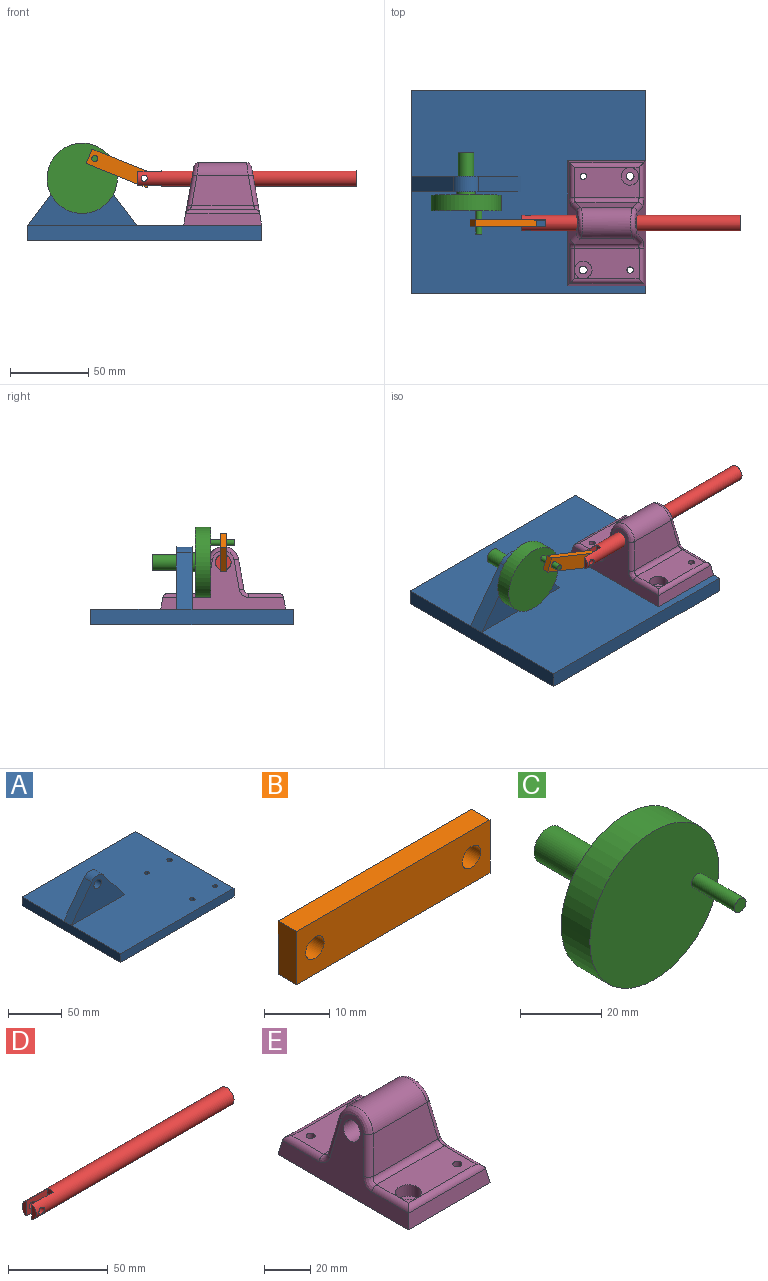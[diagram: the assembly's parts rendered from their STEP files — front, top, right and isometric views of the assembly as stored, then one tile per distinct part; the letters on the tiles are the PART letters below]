
ASSEMBLY  parts=5 mates=5
PART A: 16 faces, bbox 150x130x50 mm
  f0: plane 150x130mm, normal (0,0,1), area 18735.6mm2, adj f1,f3,f4,f5,f6,f10,f11,f12
  f1: plane 130x10mm, normal (-1,0,0), area 1300mm2, adj f0,f2,f4,f5,f8
  f2: plane 150x130mm, normal (0,0,-1), area 19435.6mm2, adj f1,f3,f4,f5,f12,f13,f14,f15
  f3: plane 130x10mm, normal (1,0,0), area 1300mm2, adj f0,f2,f4,f5
  f4: plane 150x10mm, normal (0,-1,0), area 1500mm2, adj f0,f1,f2,f3
  f5: plane 150x10mm, normal (0,1,0), area 1500mm2, adj f0,f1,f2,f3
  f6: plane 36x27mm, normal (0.8,0,0.6), area 450mm2, adj f0,f7,f10,f11
  f7: cylinder r=10mm len=16mm, axis (0,-1,0), area 185.5mm2, adj f6,f8,f10,f11
  f8: plane 36x27mm, normal (-0.8,0,0.6), area 450mm2, adj f1,f7,f10,f11
  f9: cylinder r=5mm len=10mm, axis (0,-1,0), area 314.2mm2, adj f10,f11
  f10: plane 70x40mm, normal (0,1,0), area 1514.2mm2, adj f0,f6,f7,f8,f9
  f11: plane 70x40mm, normal (0,-1,0), area 1514.2mm2, adj f0,f6,f7,f8,f9
  f12: cylinder r=2.5mm len=10mm, axis (0,0,1), area 157.1mm2, adj f0,f2
  f13: cylinder r=2.5mm len=10mm, axis (0,0,1), area 157.1mm2, adj f0,f2
  f14: cylinder r=2mm len=10mm, axis (0,0,1), area 125.7mm2, adj f0,f2
  f15: cylinder r=2mm len=10mm, axis (0,0,1), area 125.7mm2, adj f0,f2
PART B: 8 faces, bbox 42x4x10 mm
  f0: plane 42x10mm, normal (0,-1,0), area 394.9mm2, adj f1,f3,f4,f5,f6,f7
  f1: plane 42x4mm, normal (0,0,1), area 168mm2, adj f0,f2,f4,f5
  f2: plane 42x10mm, normal (0,1,0), area 394.9mm2, adj f1,f3,f4,f5,f6,f7
  f3: cylinder r=2mm len=4mm, axis (0,1,0), area 50.3mm2, adj f0,f2
  f4: plane 10x4mm, normal (-1,0,0), area 40mm2, adj f0,f1,f2,f6
  f5: plane 10x4mm, normal (1,0,0), area 40mm2, adj f0,f1,f2,f6
  f6: plane 42x4mm, normal (0,0,-1), area 168mm2, adj f0,f2,f4,f5
  f7: cylinder r=2mm len=4mm, axis (0,1,0), area 50.3mm2, adj f0,f2
PART C: 9 faces, bbox 45x52x45 mm
  f0: cylinder r=5mm len=25mm, axis (0,-1,0), area 785.4mm2, adj f1,f3
  f1: plane 10x10mm, normal (0,1,0), area 78.5mm2, adj f0
  f2: cylinder r=6mm len=12mm, axis (0,1,0), area 75.4mm2, adj f3,f6
  f3: plane 12x12mm, normal (0,1,0), area 34.6mm2, adj f0,f2
  f4: cylinder r=22.5mm len=45mm, axis (0,1,0), area 1413.7mm2, adj f5,f6
  f5: plane 45x45mm, normal (0,-1,0), area 1577.9mm2, adj f4,f7
  f6: plane 45x45mm, normal (0,1,0), area 1477.3mm2, adj f2,f4
  f7: cylinder r=2mm len=15mm, axis (0,1,0), area 188.5mm2, adj f5,f8
  f8: plane 4x4mm, normal (0,-1,0), area 12.6mm2, adj f7
PART D: 9 faces, bbox 140x10x10 mm
  f0: plane 9.17x3mm, normal (-1,0,0), area 19.8mm2, adj f1,f4
  f1: cylinder r=5mm len=140mm, axis (1,0,0), area 4249.1mm2, adj f0,f2,f3,f4,f5,f6,f7,f8
  f2: plane 9.17x3mm, normal (-1,0,0), area 19.8mm2, adj f1,f5
  f3: plane 10x10mm, normal (1,0,0), area 78.5mm2, adj f1
  f4: plane 15x9.17mm, normal (0,1,0), area 124.9mm2, adj f0,f1,f6,f8
  f5: plane 15x9.17mm, normal (0,-1,0), area 124.9mm2, adj f1,f2,f6,f7
  f6: plane 10x4mm, normal (-1,0,0), area 38.9mm2, adj f1,f4,f5
  f7: cylinder r=2mm len=4mm, axis (0,-1,0), area 35.1mm2, adj f1,f5
  f8: cylinder r=2mm len=4mm, axis (0,-1,0), area 35.1mm2, adj f1,f4
PART E: 37 faces, bbox 50.4x80.4x40.4 mm
  f0: plane 39.69x19.26mm, normal (0,0.98,0.17), area 709.7mm2, adj f3,f12,f20,f26
  f1: plane 39.69x19.26mm, normal (0,-0.98,0.17), area 709.7mm2, adj f3,f15,f23,f27
  f2: plane 80x50mm, normal (0,0,-1), area 3935.6mm2, adj f5,f6,f7,f9,f29,f32,f35,f36
  f3: cylinder r=10mm len=32.9mm, axis (1,0,0), area 882.1mm2, adj f0,f1,f11,f28
  f4: cylinder r=5mm len=41.18mm, axis (1,0,0), area 1238.4mm2, adj f5,f6
  f5: plane 80.37x37.89mm, normal (-0.98,0,0.17), area 1036.4mm2, adj f2,f4,f7,f9,f11,f12,f13,f14
  f6: plane 80x37.52mm, normal (0.98,0,0.17), area 1036.4mm2, adj f2,f4,f7,f9,f21,f22,f24,f25
  f7: plane 50x7.52mm, normal (0,-0.98,0.17), area 371.7mm2, adj f2,f5,f6,f18
  f8: plane 41.44x19.52mm, normal (0,0,1), area 697mm2, adj f14,f18,f22,f23,f31,f36
  f9: plane 50x7.52mm, normal (0,0.98,0.17), area 371.7mm2, adj f2,f5,f6,f17
  f10: plane 41.44x19.52mm, normal (0,0,1), area 697mm2, adj f13,f17,f20,f21,f34,f35
  f11: bspline ~19.7x8.26mm, area 107.6mm2, adj f3,f5,f12,f15
  f12: cylinder r=3mm len=19.46mm, axis (0.17,-0.17,0.97), area 91.7mm2, adj f0,f5,f11,f16
  f13: cylinder r=3mm len=22.48mm, axis (0,-1,0), area 89.2mm2, adj f5,f10,f16,f17
  f14: cylinder r=3mm len=22.48mm, axis (0,-1,0), area 89.2mm2, adj f5,f8,f18,f19
  f15: cylinder r=3mm len=19.46mm, axis (-0.17,-0.17,-0.97), area 91.7mm2, adj f1,f5,f11,f19
  f16: bspline ~5.91x5.15mm, area 25.6mm2, adj f5,f12,f13,f20
  f17: cylinder r=3mm len=47.35mm, axis (1,0,0), area 188.5mm2, adj f9,f10,f13,f21
  f18: cylinder r=3mm len=47.35mm, axis (1,0,0), area 188.5mm2, adj f7,f8,f14,f22
  f19: bspline ~5.91x5.15mm, area 25.6mm2, adj f5,f14,f15,f23
  f20: cylinder r=3mm len=41.44mm, axis (-1,0,0), area 169.9mm2, adj f0,f10,f16,f24
  f21: cylinder r=3mm len=22.48mm, axis (0,-1,0), area 89.2mm2, adj f6,f10,f17,f24
  f22: cylinder r=3mm len=22.48mm, axis (0,-1,0), area 89.2mm2, adj f6,f8,f18,f25
  f23: cylinder r=3mm len=41.44mm, axis (1,0,0), area 169.9mm2, adj f1,f8,f19,f25
  f24: bspline ~5.91x5.15mm, area 25.6mm2, adj f6,f20,f21,f26
  f25: bspline ~5.91x5.15mm, area 25.6mm2, adj f6,f22,f23,f27
  f26: cylinder r=3mm len=19.46mm, axis (-0.17,-0.17,0.97), area 91.7mm2, adj f0,f6,f24,f28
  f27: cylinder r=3mm len=19.46mm, axis (0.17,-0.17,-0.97), area 91.7mm2, adj f1,f6,f25,f28
  f28: bspline ~19.94x9.13mm, area 107.6mm2, adj f3,f6,f26,f27
  f29: cylinder r=2.5mm len=5mm, axis (0,0,1), area 62.8mm2, adj f2,f30
  f30: plane 11.25x11.25mm, normal (0,0,1), area 79.8mm2, adj f29,f31
  f31: cylinder r=5.62mm len=11.25mm, axis (0,0,1), area 212.1mm2, adj f8,f30
  f32: cylinder r=2.5mm len=5mm, axis (0,0,1), area 62.8mm2, adj f2,f33
  f33: plane 11.25x11.25mm, normal (0,0,1), area 79.8mm2, adj f32,f34
  f34: cylinder r=5.62mm len=11.25mm, axis (0,0,1), area 212.1mm2, adj f10,f33
  f35: cylinder r=2mm len=10mm, axis (0,0,1), area 125.7mm2, adj f2,f10
  f36: cylinder r=2mm len=10mm, axis (0,0,1), area 125.7mm2, adj f2,f8
PLACE A at identity fixed
PLACE B rot(axis=(0,1,0),21.8deg) t=(-19.78,0,5.48)mm
PLACE C rot(axis=(0,-1,0),57.2deg) t=(6.88,0,47.37)mm
PLACE D t=(-9.3,0,0)mm
PLACE E at identity
MATE revolute D.f7 <-> B.f3  axis (0,1,0) through (-0.3,-22,30)mm
MATE cylindrical D.f1 <-> E.f3  axis (1,0,0) through (65.7,-20,30)mm
MATE fastened A.f12 <-> E.f29  axis (0,0,1) through (35,-50,0)mm
MATE revolute A.f7 <-> C.f0  axis (0,-1,0) through (-40,0,30)mm
MATE cylindrical B.f7 <-> C.f7  axis (0,-1,0) through (-31.87,-22,42.61)mm
